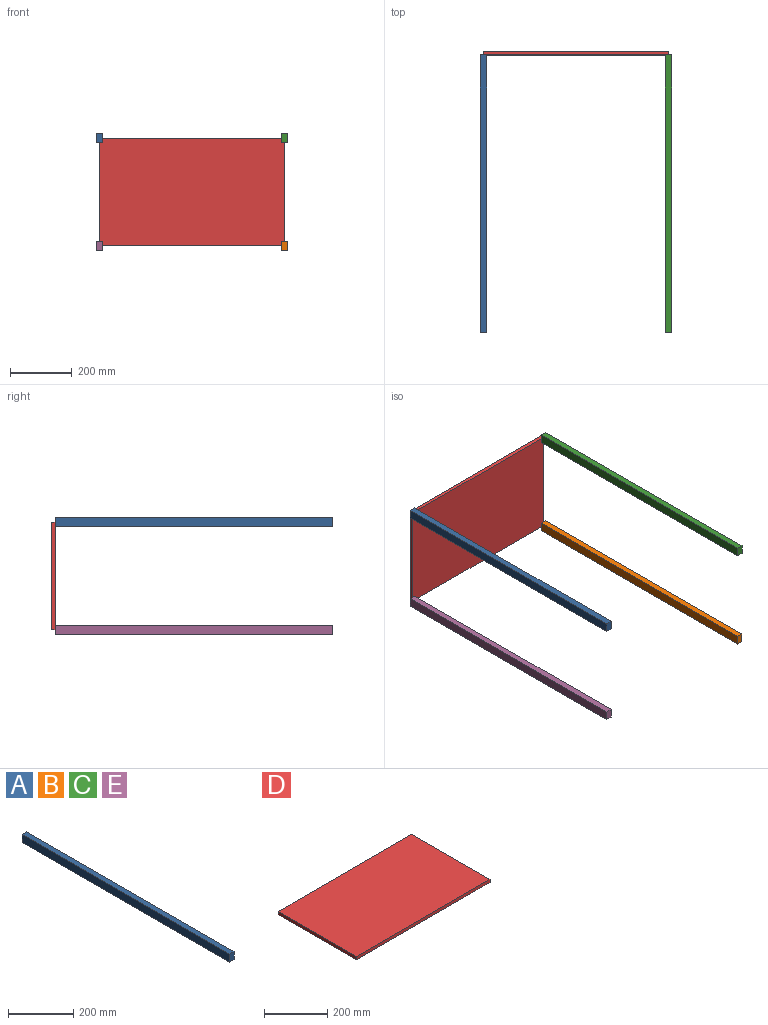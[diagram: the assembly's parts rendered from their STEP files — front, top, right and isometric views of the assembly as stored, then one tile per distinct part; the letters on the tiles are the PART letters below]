
ASSEMBLY  parts=5 mates=4
PART A: 6 faces, bbox 20x900x30 mm
  f0: plane 900x30mm, normal (-1,0,0), area 27000mm2, adj f1,f3,f4,f5
  f1: plane 30x20mm, normal (0,-1,0), area 600mm2, adj f0,f2,f4,f5
  f2: plane 900x30mm, normal (1,0,0), area 27000mm2, adj f1,f3,f4,f5
  f3: plane 30x20mm, normal (0,1,0), area 600mm2, adj f0,f2,f4,f5
  f4: plane 900x20mm, normal (0,0,1), area 18000mm2, adj f0,f1,f2,f3
  f5: plane 900x20mm, normal (0,0,-1), area 18000mm2, adj f0,f1,f2,f3
PART B: same geometry as A
PART C: same geometry as A
PART D: 6 faces, bbox 600x350x12 mm
  f0: plane 350x12mm, normal (-1,0,0), area 4200mm2, adj f1,f3,f4,f5
  f1: plane 600x12mm, normal (0,-1,0), area 7200mm2, adj f0,f2,f4,f5
  f2: plane 350x12mm, normal (1,0,0), area 4200mm2, adj f1,f3,f4,f5
  f3: plane 600x12mm, normal (0,1,0), area 7200mm2, adj f0,f2,f4,f5
  f4: plane 600x350mm, normal (0,0,1), area 210000mm2, adj f0,f1,f2,f3
  f5: plane 600x350mm, normal (0,0,-1), area 210000mm2, adj f0,f1,f2,f3
PART E: same geometry as A
PLACE A t=(-647.92,-116.8,-850.58)mm
PLACE B t=(-47.92,-116.8,-1200.58)mm
PLACE C t=(-47.92,-116.8,-850.58)mm fixed
PLACE D rot(axis=(0,-0.71,0.71),180deg) t=(-37.92,795.2,164.42)mm
PLACE E t=(-647.92,-116.8,-1200.58)mm
MATE fastened E.f3 <-> D.f4  axis (0,1,0) through (-637.92,783.2,-1185.58)mm
MATE fastened C.f3 <-> D.f4  axis (0,1,0) through (-37.92,783.2,-835.58)mm
MATE revolute B.f3 <-> D.f4  axis (0,1,0) through (-37.92,783.2,-1185.58)mm
MATE fastened A.f3 <-> D.f4  axis (0,1,0) through (-637.92,783.2,-835.58)mm
